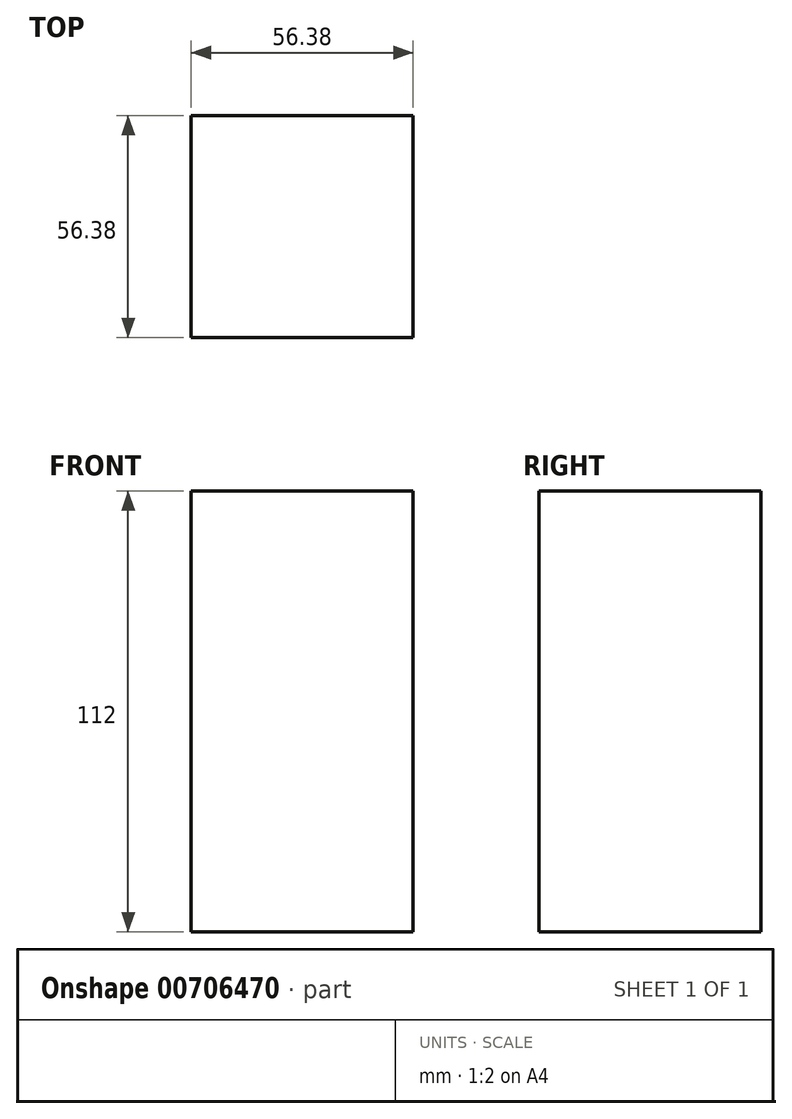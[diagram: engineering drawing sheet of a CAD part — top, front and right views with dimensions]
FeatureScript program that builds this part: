
annotation { "Feature Type Name" : "Feature", "Feature Type Description" : "" }
export const myFeature = defineFeature(function(context is Context, id is Id, definition is map)
    precondition{}
    {
        {
            var Q0;
            Q0=qCreatedBy(makeId("Top.planeOp"),FACE);
            var sketch = newSketch(context, id + "F0", { "sketchPlane" : qUnion([Q0])});
            skLineSegment(sketch, "E0.bottom", {"start": v(-28.2, 28.2) * mm, "end": v(28.2, 28.2) * mm});
            skLineSegment(sketch, "E0.top", {"start": v(-28.2, -28.2) * mm, "end": v(28.2, -28.2) * mm});
            skLineSegment(sketch, "E0.left", {"start": v(-28.2, 28.2) * mm, "end": v(-28.2, -28.2) * mm});
            skLineSegment(sketch, "E0.right", {"start": v(28.2, 28.2) * mm, "end": v(28.2, -28.2) * mm});
            skPoint(sketch, "E1", {"position": v(0, 28.2) * mm});
            skPoint(sketch, "E2", {"position": v(28.2, 0) * mm});
            skSolve(sketch);
        }
        {
            var Q0;
            Q0 = qSketchRegion(id + "F0", true);
            extrude(context, id + "F1", {"entities" : qUnion([Q0]), "depth" : 112 * mm, "offsetDistance" : 25.4 * mm});
        }
    });
